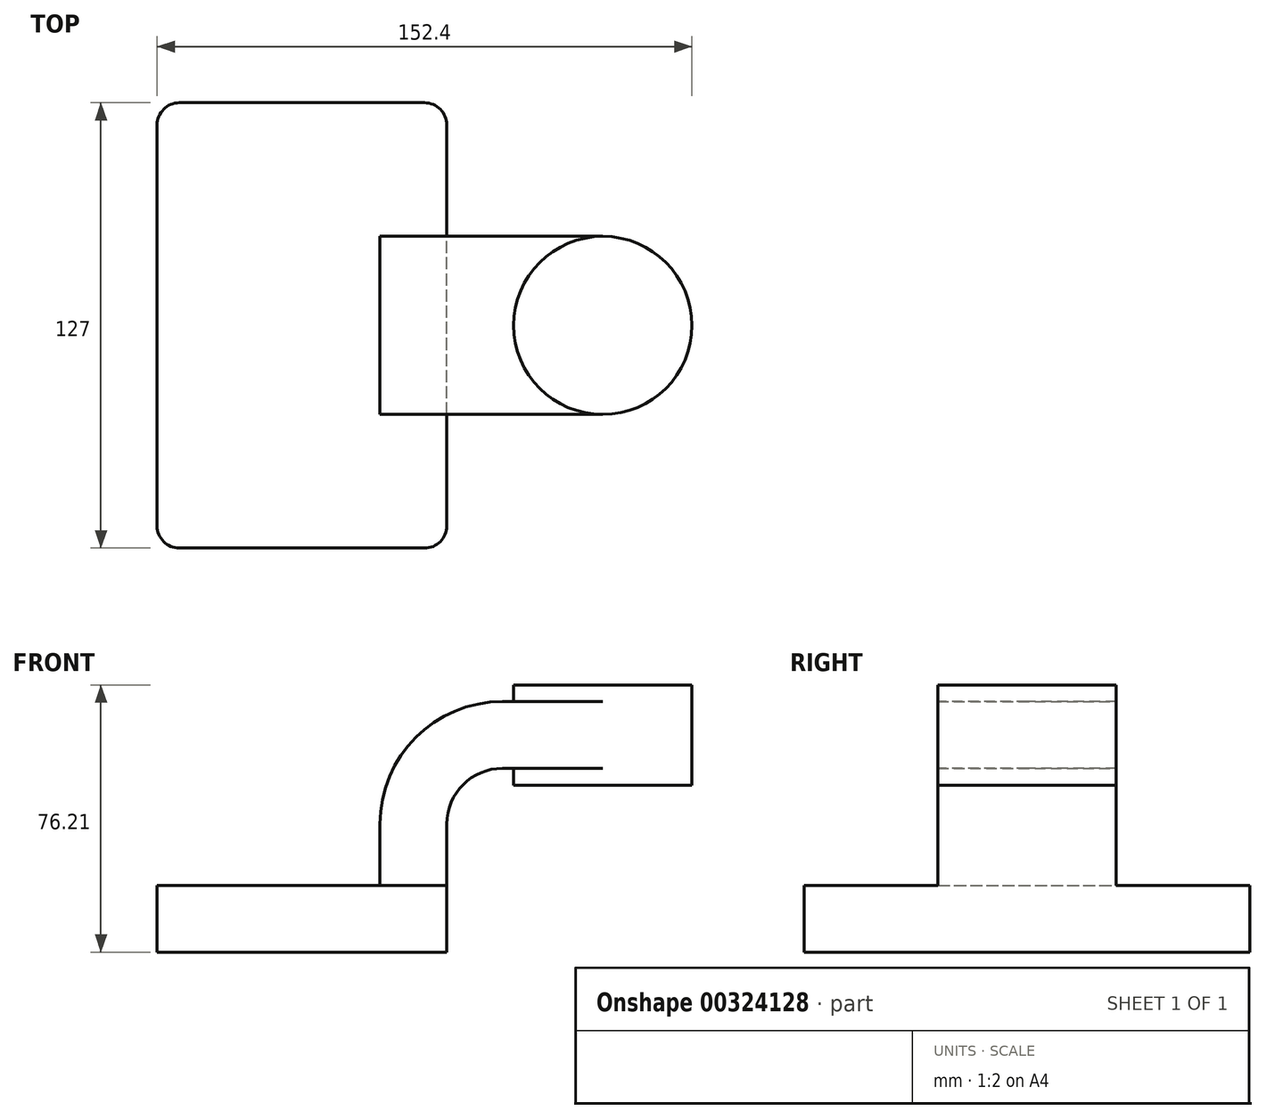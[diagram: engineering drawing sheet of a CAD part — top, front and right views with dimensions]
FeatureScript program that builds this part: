
annotation { "Feature Type Name" : "Feature", "Feature Type Description" : "" }
export const myFeature = defineFeature(function(context is Context, id is Id, definition is map)
    precondition{}
    {
        {
            var Q0;
            Q0=qCreatedBy(makeId("Front.planeOp"),FACE);
            var sketch = newSketch(context, id + "F0", { "sketchPlane" : qUnion([Q0])});
            skLineSegment(sketch, "E0.bottom", {"start": v(41.28, -9.52) * mm, "end": v(-41.28, -9.53) * mm});
            skLineSegment(sketch, "E0.top", {"start": v(41.28, 9.53) * mm, "end": v(-41.28, 9.53) * mm});
            skLineSegment(sketch, "E0.left", {"start": v(41.28, -9.52) * mm, "end": v(41.28, 9.53) * mm});
            skLineSegment(sketch, "E0.right", {"start": v(-41.28, -9.53) * mm, "end": v(-41.28, 9.53) * mm});
            skPoint(sketch, "E0.middle", {"position": v(0, 0) * mm});
            skLineSegment(sketch, "E1.bottom", {"start": v(111.12, 66.68) * mm, "end": v(60.33, 66.68) * mm});
            skLineSegment(sketch, "E1.top", {"start": v(111.12, 38.1) * mm, "end": v(60.33, 38.1) * mm});
            skLineSegment(sketch, "E1.left", {"start": v(111.12, 66.67) * mm, "end": v(111.12, 38.1) * mm});
            skLineSegment(sketch, "E1.right", {"start": v(60.33, 66.67) * mm, "end": v(60.33, 38.1) * mm});
            skPoint(sketch, "E1.middle", {"position": v(85.73, 52.39) * mm});
            skLineSegment(sketch, "E2", {"start": v(41.28, 9.53) * mm, "end": v(41.28, 27) * mm});
            skArc(sketch, "E3", {"start": v(41.27, 27) * mm, "mid": v(45.92, 38.23) * mm, "end": v(57.15, 42.88) * mm});
            skLineSegment(sketch, "E4", {"start": v(57.15, 42.88) * mm, "end": v(85.72, 42.88) * mm});
            skLineSegment(sketch, "E5.0", {"start": v(57.15, 61.93) * mm, "end": v(85.72, 61.93) * mm});
            skArc(sketch, "E5.1", {"start": v(22.23, 27) * mm, "mid": v(32.45, 51.7) * mm, "end": v(57.15, 61.93) * mm});
            skLineSegment(sketch, "E5.2", {"start": v(22.22, 9.53) * mm, "end": v(22.22, 27) * mm});
            skLineSegment(sketch, "E6", {"start": v(85.72, 42.88) * mm, "end": v(85.73, 66.68) * mm});
            skFitSpline(sketch, "E7", {"points": [v(-41.28, 9.52) * mm, v(57.15, 61.93) * mm], "startDerivative": vector(17.6, 99.93) * mm, "endDerivative": vector(127.76, -1.85) * mm});
            skLineSegment(sketch, "E8", {"start": v(85.72, 42.88) * mm, "end": v(85.73, 38.1) * mm});
            skSolve(sketch);
        }
        {
            var Q0;
            Q0=makeQuery(id+"F0.imprint","IMPRINT",FACE,{"disambiguationData":[TD([[makeQuery(id+"F0.imprint","IMPRINT",EDGE,{"derivedFrom":sQuery(id+"F0.wireOp",EDGE,"E0.bottom")}),-1.0]])]});
            extrude(context, id + "F1", {"entities" : qUnion([Q0]), "endBound" : BoundingType.SYMMETRIC, "depth" : 127 * mm});
        }
        {
            var Q0;
            {var subQ1=sQuery(id+"F0.wireOp",EDGE,"E2");Q0=makeQuery(id+"F0.imprint","IMPRINT",FACE,{"disambiguationData":[TD([[makeQuery(id+"F0.imprint","IMPRINT",EDGE,{"derivedFrom":subQ1}),1.0]])]});}
            var Q1;
            {var subQ0=sQuery(id+"F0.wireOp",EDGE,"E5.0");var subQ1=sQuery(id+"F0.wireOp",EDGE,"E1.right");var subQ2=makeQuery(id+"F0.imprint","INTERSECT",VERTEX,{"derivedFrom":[subQ1,subQ0]});Q1=makeQuery(id+"F0.imprint","IMPRINT",FACE,{"disambiguationData":[TD([[makeQuery(id+"F0.imprint","IMPRINT",EDGE,{"disambiguationData":[TD([[subQ2,-1.0]])],"derivedFrom":subQ1}),1.0]])]});}
            extrude(context, id + "F2", {"entities" : qUnion([Q0, Q1]), "operationType" : NewBodyOperationType.ADD, "endBound" : BoundingType.SYMMETRIC, "depth" : 50.8 * mm});
        }
        {
            var Q0;
            Q0=makeQuery(id+"F0.imprint","IMPRINT",FACE,{"disambiguationData":[TD([[makeQuery(id+"F0.imprint","IMPRINT",EDGE,{"derivedFrom":sQuery(id+"F0.wireOp",EDGE,"E5.1")}),1.0]])]});
            extrude(context, id + "F3", {"entities" : qUnion([Q0]), "operationType" : NewBodyOperationType.ADD, "endBound" : BoundingType.SYMMETRIC, "depth" : 15.88 * mm});
        }
        {
            var Q0;
            {var subQ3=sQuery(id+"F0.wireOp",EDGE,"E1.left");Q0=makeQuery(id+"F0.imprint","IMPRINT",FACE,{"disambiguationData":[TD([[makeQuery(id+"F0.imprint","IMPRINT",EDGE,{"derivedFrom":subQ3}),-1.0]])]});}
            var Q1;
            Q1=sQuery(id+"F0.wireOp",EDGE,"E6");
            revolve(context, id + "F4", {"operationType" : NewBodyOperationType.ADD, "entities" : qUnion([Q0]), "axis" : qUnion([Q1]), "revolveType" : RevolveType.FULL});
        }
        {
            var Q0;
            Q0=makeQuery(id+"F1.opExtrude","CAP_EDGE",EDGE,{"disambiguationData":[OSD([sQuery(id+"F0.wireOp",EDGE,"E0.right")])],"isStart":false});
            var Q1;
            Q1=makeQuery(id+"F1.opExtrude","CAP_EDGE",EDGE,{"disambiguationData":[OSD([sQuery(id+"F0.wireOp",EDGE,"E0.left")])],"isStart":false});
            var Q2;
            Q2=makeQuery(id+"F1.opExtrude","CAP_EDGE",EDGE,{"disambiguationData":[OSD([sQuery(id+"F0.wireOp",EDGE,"E0.left")])],"isStart":true});
            var Q3;
            Q3=makeQuery(id+"F1.opExtrude","CAP_EDGE",EDGE,{"disambiguationData":[OSD([sQuery(id+"F0.wireOp",EDGE,"E0.right")])],"isStart":true});
            fillet(context, id + "F5", {"entities" : qUnion([Q0, Q1, Q2, Q3]), "radius" : 6.35 * mm, "tangentPropagation" : true, "allowEdgeOverflow" : false});
        }
    });
